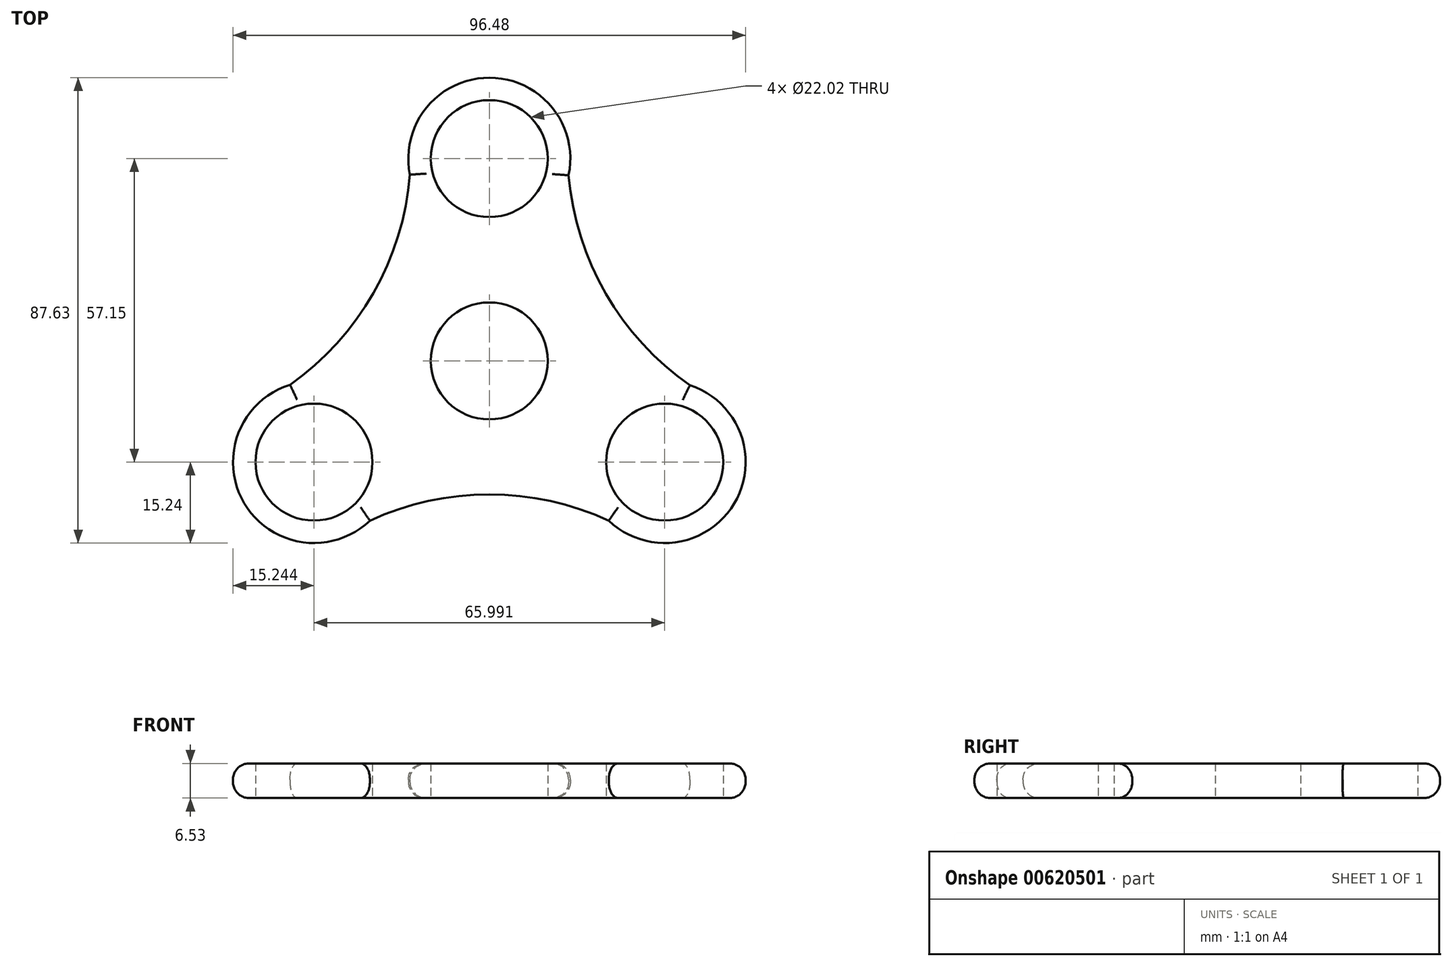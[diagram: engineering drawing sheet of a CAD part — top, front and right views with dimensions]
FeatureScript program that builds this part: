
annotation { "Feature Type Name" : "Feature", "Feature Type Description" : "" }
export const myFeature = defineFeature(function(context is Context, id is Id, definition is map)
    precondition{}
    {
        {
            var Q0;
            Q0=qCreatedBy(makeId("Top.planeOp"),FACE);
            var sketch = newSketch(context, id + "F0", { "sketchPlane" : qUnion([Q0])});
            skCircle(sketch, "E0", {"center": v(0, 0) * mm, "radius": 11.01 * mm});
            skCircle(sketch, "E1", {"center": v(33, -19.05) * mm, "radius": 11.01 * mm});
            skCircle(sketch, "E2", {"center": v(0, 38.1) * mm, "radius": 11.01 * mm});
            skCircle(sketch, "E3", {"center": v(-33, -19.05) * mm, "radius": 11.01 * mm});
            skArc(sketch, "E4", {"start": v(-37.53, -4.5) * mm, "mid": v(-46.13, -26.78) * mm, "end": v(-22.47, -30.08) * mm});
            skArc(sketch, "E5", {"start": v(22.47, -30.08) * mm, "mid": v(46.07, -26.88) * mm, "end": v(37.75, -4.57) * mm});
            skArc(sketch, "E6", {"start": v(14.92, 34.98) * mm, "mid": v(0.05, 53.34) * mm, "end": v(-14.94, 35.08) * mm});
            skPoint(sketch, "E7", {"position": v(-22.47, -30.08) * mm});
            skPoint(sketch, "E8", {"position": v(22.47, -30.08) * mm});
            skArc(sketch, "E9", {"start": v(22.47, -30.08) * mm, "mid": v(0, -25.15) * mm, "end": v(-22.47, -30.08) * mm});
            skArc(sketch, "E10", {"start": v(-37.53, -4.5) * mm, "mid": v(-21.83, 12.77) * mm, "end": v(-14.94, 35.08) * mm});
            skArc(sketch, "E11", {"start": v(14.92, 34.98) * mm, "mid": v(21.92, 12.66) * mm, "end": v(37.75, -4.57) * mm});
            skSolve(sketch);
        }
        {
            var Q0;
            Q0=makeQuery(id+"F0.imprint","IMPRINT",FACE,{"disambiguationData":[TD([[makeQuery(id+"F0.imprint","IMPRINT",EDGE,{"derivedFrom":sQuery(id+"F0.wireOp",EDGE,"E0")}),-1.0]])]});
            var Q1;
            Q1=makeQuery(id+"F0.imprint","IMPRINT",FACE,{"disambiguationData":[TD([[makeQuery(id+"F0.imprint","IMPRINT",EDGE,{"derivedFrom":sQuery(id+"F0.wireOp",EDGE,"E3")}),-1.0]])]});
            var Q2;
            Q2=makeQuery(id+"F0.imprint","IMPRINT",FACE,{"disambiguationData":[TD([[makeQuery(id+"F0.imprint","IMPRINT",EDGE,{"derivedFrom":sQuery(id+"F0.wireOp",EDGE,"E2")}),-1.0]])]});
            var Q3;
            Q3=makeQuery(id+"F0.imprint","IMPRINT",FACE,{"disambiguationData":[TD([[makeQuery(id+"F0.imprint","IMPRINT",EDGE,{"derivedFrom":sQuery(id+"F0.wireOp",EDGE,"E1")}),-1.0]])]});
            extrude(context, id + "F1", {"entities" : qUnion([Q0, Q1, Q2, Q3]), "depth" : 6.53 * mm, "offsetDistance" : 25.4 * mm});
        }
        {
            var Q0;
            Q0=makeQuery(id+"F1.opExtrude","CAP_EDGE",EDGE,{"disambiguationData":[OSD([sQuery(id+"F0.wireOp",EDGE,"E6")])],"isStart":false});
            var Q1;
            Q1=makeQuery(id+"F1.opExtrude","CAP_EDGE",EDGE,{"disambiguationData":[OSD([sQuery(id+"F0.wireOp",EDGE,"E10")])],"isStart":false});
            var Q2;
            Q2=makeQuery(id+"F1.opExtrude","CAP_EDGE",EDGE,{"disambiguationData":[OSD([sQuery(id+"F0.wireOp",EDGE,"E4")])],"isStart":false});
            var Q3;
            Q3=makeQuery(id+"F1.opExtrude","CAP_EDGE",EDGE,{"disambiguationData":[OSD([sQuery(id+"F0.wireOp",EDGE,"E9")])],"isStart":false});
            var Q4;
            Q4=makeQuery(id+"F1.opExtrude","CAP_EDGE",EDGE,{"disambiguationData":[OSD([sQuery(id+"F0.wireOp",EDGE,"E5")])],"isStart":false});
            var Q5;
            Q5=makeQuery(id+"F1.opExtrude","CAP_EDGE",EDGE,{"disambiguationData":[OSD([sQuery(id+"F0.wireOp",EDGE,"E11")])],"isStart":false});
            fillet(context, id + "F2", {"entities" : qUnion([Q0, Q1, Q2, Q3, Q4, Q5]), "radius" : 3.05 * mm, "tangentPropagation" : true, "allowEdgeOverflow" : false});
        }
        {
            var Q0;
            Q0=makeQuery(id+"F1.opExtrude","CAP_EDGE",EDGE,{"disambiguationData":[OSD([sQuery(id+"F0.wireOp",EDGE,"E11")])],"isStart":true});
            var Q1;
            Q1=makeQuery(id+"F1.opExtrude","CAP_EDGE",EDGE,{"disambiguationData":[OSD([sQuery(id+"F0.wireOp",EDGE,"E5")])],"isStart":true});
            var Q2;
            Q2=makeQuery(id+"F1.opExtrude","CAP_EDGE",EDGE,{"disambiguationData":[OSD([sQuery(id+"F0.wireOp",EDGE,"E9")])],"isStart":true});
            var Q3;
            Q3=makeQuery(id+"F1.opExtrude","CAP_EDGE",EDGE,{"disambiguationData":[OSD([sQuery(id+"F0.wireOp",EDGE,"E4")])],"isStart":true});
            var Q4;
            Q4=makeQuery(id+"F1.opExtrude","CAP_EDGE",EDGE,{"disambiguationData":[OSD([sQuery(id+"F0.wireOp",EDGE,"E10")])],"isStart":true});
            var Q5;
            Q5=makeQuery(id+"F1.opExtrude","CAP_EDGE",EDGE,{"disambiguationData":[OSD([sQuery(id+"F0.wireOp",EDGE,"E6")])],"isStart":true});
            fillet(context, id + "F3", {"entities" : qUnion([Q0, Q1, Q2, Q3, Q4, Q5]), "radius" : 3.05 * mm, "tangentPropagation" : true, "allowEdgeOverflow" : false});
        }
    });
